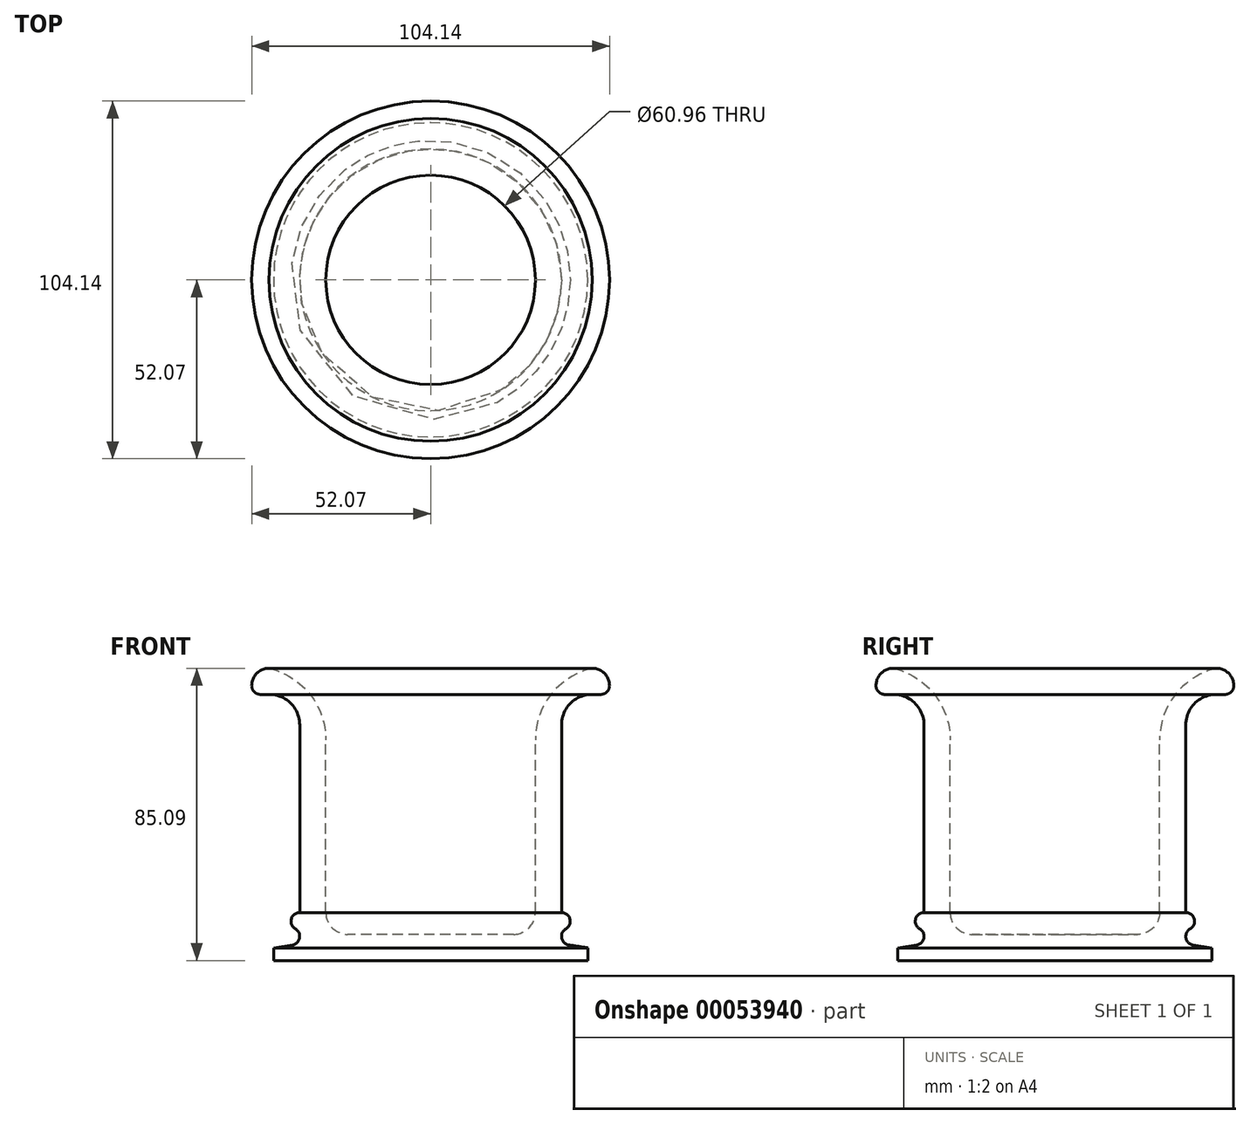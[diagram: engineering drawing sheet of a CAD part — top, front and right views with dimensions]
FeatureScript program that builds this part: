
annotation { "Feature Type Name" : "Feature", "Feature Type Description" : "" }
export const myFeature = defineFeature(function(context is Context, id is Id, definition is map)
    precondition{}
    {
        {
            var Q0;
            Q0=qCreatedBy(makeId("Front.planeOp"),FACE);
            var sketch = newSketch(context, id + "F0", { "sketchPlane" : qUnion([Q0])});
            skLineSegment(sketch, "E0.top", {"start": v(-38.1, -21.82) * mm, "end": v(-30.48, -21.82) * mm});
            skLineSegment(sketch, "E0.left", {"start": v(-38.1, 46.76) * mm, "end": v(-38.1, -7.85) * mm});
            skLineSegment(sketch, "E0.right", {"start": v(-30.48, 42.4) * mm, "end": v(-30.48, -7.85) * mm});
            skLineSegment(sketch, "E1.bottom", {"start": v(0, -21.82) * mm, "end": v(-38.1, -21.82) * mm});
            skLineSegment(sketch, "E1.top", {"start": v(0, -14.2) * mm, "end": v(-24.13, -14.2) * mm});
            skLineSegment(sketch, "E1.left", {"start": v(0, -21.82) * mm, "end": v(0, -14.2) * mm});
            skPoint(sketch, "E2.visualSharp", {"position": v(-30.48, -14.2) * mm});
            skArc(sketch, "E2.filletArc", {"start": v(-30.48, -7.85) * mm, "mid": v(-28.62, -12.34) * mm, "end": v(-24.13, -14.2) * mm});
            skLineSegment(sketch, "E3.top", {"start": v(-47, 55.65) * mm, "end": v(-49.53, 55.65) * mm});
            skLineSegment(sketch, "E3.right", {"start": v(-52.07, 58.19) * mm, "end": v(-52.07, 58.19) * mm});
            skPoint(sketch, "E4.visualSharp", {"position": v(-30.48, 67.08) * mm});
            skPoint(sketch, "E5.visualSharp", {"position": v(-52.07, 63.27) * mm});
            skArc(sketch, "E5.filletArc", {"start": v(-47, 63.27) * mm, "mid": v(-50.59, 61.78) * mm, "end": v(-52.07, 58.19) * mm});
            skPoint(sketch, "E6.visualSharp", {"position": v(-52.07, 55.65) * mm});
            skArc(sketch, "E6.filletArc", {"start": v(-52.07, 58.19) * mm, "mid": v(-51.33, 56.4) * mm, "end": v(-49.53, 55.65) * mm});
            skPoint(sketch, "E7.visualSharp", {"position": v(-38.1, 55.65) * mm});
            skArc(sketch, "E7.filletArc", {"start": v(-38.1, 46.76) * mm, "mid": v(-40.7, 53.04) * mm, "end": v(-47, 55.65) * mm});
            skArc(sketch, "E8", {"start": v(-30.48, 42.4) * mm, "mid": v(-35.11, 55.71) * mm, "end": v(-47, 63.27) * mm});
            skLineSegment(sketch, "E9.bottom", {"start": v(-38.1, -21.82) * mm, "end": v(-45.72, -21.82) * mm});
            skArc(sketch, "E10", {"start": v(-38.1, -7.85) * mm, "mid": v(-40.64, -10.39) * mm, "end": v(-38.1, -12.93) * mm});
            skArc(sketch, "E11", {"start": v(-40.25, -17.3) * mm, "mid": v(-38.14, -15.25) * mm, "end": v(-39.37, -12.59) * mm});
            skLineSegment(sketch, "E12", {"start": v(-45.72, -21.82) * mm, "end": v(-45.72, -18.14) * mm});
            skLineSegment(sketch, "E13", {"start": v(-45.72, -18.14) * mm, "end": v(-40.25, -17.3) * mm});
            skPoint(sketch, "E9.left.end.orphan", {"position": v(-33.88, -14.79) * mm});
            skSolve(sketch);
        }
        {
            var Q0;
            Q0=qCreatedBy(makeId("Front.planeOp"),FACE);
            var sketch = newSketch(context, id + "F1", { "sketchPlane" : qUnion([Q0])});
            skLineSegment(sketch, "E14", {"start": v(0, 72.82) * mm, "end": v(0, -55.65) * mm});
            skSolve(sketch);
        }
        {
            var Q0;
            Q0=makeQuery(id+"F0.imprint","IMPRINT",FACE,{"disambiguationData":[TD([[makeQuery(id+"F0.imprint","IMPRINT",EDGE,{"derivedFrom":sQuery(id+"F0.wireOp",EDGE,"E0.left")}),1.0]])]});
            var Q1;
            Q1 = qSketchRegion(id + "F1", true);
            var Q2;
            Q2=sQuery(id+"F1.wireOp",EDGE,"E14");
            revolve(context, id + "F2", {"entities" : qUnion([Q0, Q1]), "axis" : qUnion([Q2]), "revolveType" : RevolveType.ONE_DIRECTION, "angle" : 360 * degree});
        }
    });
